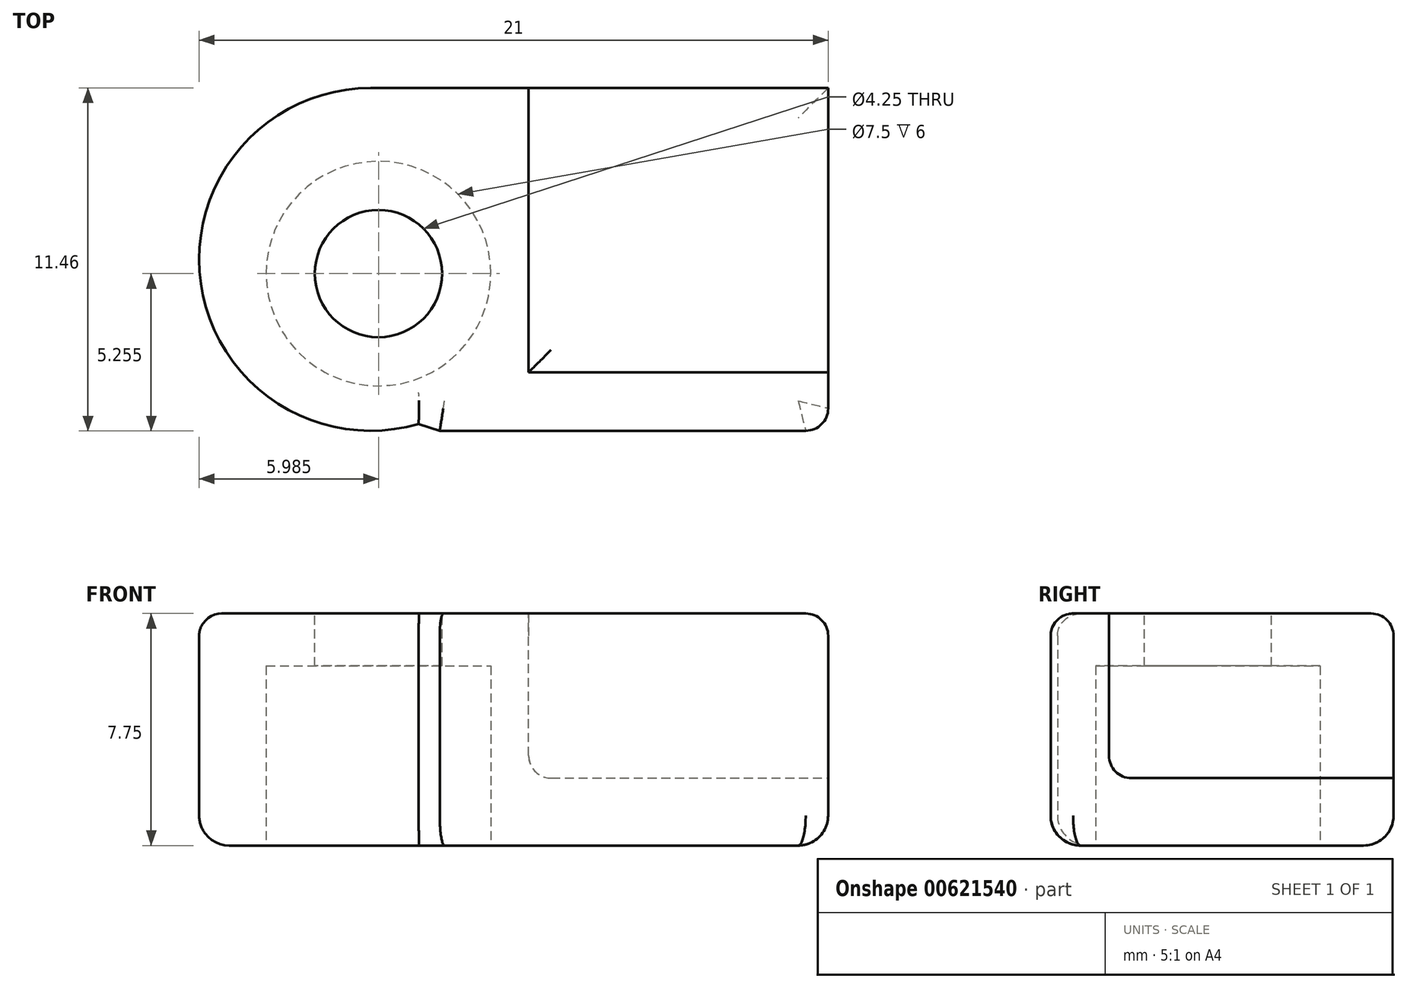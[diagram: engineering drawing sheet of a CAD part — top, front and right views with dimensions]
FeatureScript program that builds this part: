
annotation { "Feature Type Name" : "Feature", "Feature Type Description" : "" }
export const myFeature = defineFeature(function(context is Context, id is Id, definition is map)
    precondition{}
    {
        {
            var Q0;
            Q0=qCreatedBy(makeId("Top.planeOp"),FACE);
            var sketch = newSketch(context, id + "F0", { "sketchPlane" : qUnion([Q0])});
            skLineSegment(sketch, "E0.bottom", {"start": v(-6.14, -5.73) * mm, "end": v(6.83, -5.73) * mm});
            skLineSegment(sketch, "E0.top", {"start": v(-8.45, 5.73) * mm, "end": v(6.83, 5.73) * mm});
            skLineSegment(sketch, "E0.right", {"start": v(6.83, -5.73) * mm, "end": v(6.83, 5.73) * mm});
            skLineSegment(sketch, "E1", {"start": v(0, 23.22) * mm, "end": v(0, -32.08) * mm, "construction": true});
            skLineSegment(sketch, "E2", {"start": v(-40.7, 0) * mm, "end": v(47.24, 0) * mm, "construction": true});
            skArc(sketch, "E3", {"start": v(-8.45, 5.72) * mm, "mid": v(-14.11, -0.81) * mm, "end": v(-6.84, -5.5) * mm});
            skLineSegment(sketch, "E4", {"start": v(-6.84, -5.5) * mm, "end": v(-6.14, -5.73) * mm});
            skSolve(sketch);
        }
        {
            var Q0;
            Q0=makeQuery(id+"F0.imprint","IMPRINT",FACE,{"disambiguationData":[TD([[makeQuery(id+"F0.imprint","IMPRINT",EDGE,{"derivedFrom":sQuery(id+"F0.wireOp",EDGE,"E0.bottom")}),1.0]])]});
            extrude(context, id + "F1", {"entities" : qUnion([Q0]), "depth" : 7.75 * mm, "offsetDistance" : 25 * mm});
        }
        {
            var Q0;
            Q0=makeQuery(id+"F1.opExtrude","CAP_FACE",FACE,{"disambiguationData":[OSD([sQuery(id+"F0.wireOp",EDGE,"E0.bottom"),sQuery(id+"F0.wireOp",EDGE,"E0.top"),sQuery(id+"F0.wireOp",EDGE,"E0.right"),sQuery(id+"F0.wireOp",EDGE,"E3")])],"isStart":false});
            var sketch = newSketch(context, id + "F2", { "sketchPlane" : qUnion([Q0])});
            skCircle(sketch, "E5", {"center": v(-8.19, -0.48) * mm, "radius": 2.12 * mm});
            skSolve(sketch);
        }
        {
            var Q0;
            Q0=makeQuery(id+"F2.imprint","IMPRINT",FACE,{"disambiguationData":[TD([[makeQuery(id+"F2.imprint","IMPRINT",EDGE,{"derivedFrom":sQuery(id+"F2.wireOp",EDGE,"E5")}),1.0]])]});
            extrude(context, id + "F3", {"entities" : qUnion([Q0]), "operationType" : NewBodyOperationType.REMOVE, "endBound" : BoundingType.THROUGH_ALL, "oppositeDirection" : true, "depth" : 25 * mm, "offsetDistance" : 25 * mm});
        }
        {
            var Q0;
            Q0=makeQuery(id+"F1.opExtrude","CAP_FACE",FACE,{"disambiguationData":[OSD([sQuery(id+"F0.wireOp",EDGE,"E0.bottom"),sQuery(id+"F0.wireOp",EDGE,"E0.top"),sQuery(id+"F0.wireOp",EDGE,"E0.right"),sQuery(id+"F0.wireOp",EDGE,"E3")])],"isStart":false});
            var sketch = newSketch(context, id + "F4", { "sketchPlane" : qUnion([Q0])});
            skLineSegment(sketch, "E6.bottom", {"start": v(6.83, 5.73) * mm, "end": v(-3.17, 5.73) * mm});
            skLineSegment(sketch, "E6.top", {"start": v(6.83, -3.77) * mm, "end": v(-3.17, -3.77) * mm});
            skLineSegment(sketch, "E6.left", {"start": v(6.83, 5.73) * mm, "end": v(6.83, -3.77) * mm});
            skLineSegment(sketch, "E6.right", {"start": v(-3.17, 5.72) * mm, "end": v(-3.17, -3.77) * mm});
            skSolve(sketch);
        }
        {
            var Q0;
            Q0=makeQuery(id+"F4.imprint","IMPRINT",FACE,{"disambiguationData":[TD([[makeQuery(id+"F4.imprint","IMPRINT",EDGE,{"derivedFrom":sQuery(id+"F4.wireOp",EDGE,"E6.bottom")}),-1.0]])]});
            extrude(context, id + "F5", {"entities" : qUnion([Q0]), "operationType" : NewBodyOperationType.REMOVE, "oppositeDirection" : true, "depth" : 5.5 * mm, "offsetDistance" : 25 * mm});
        }
        {
            var Q0;
            Q0=makeQuery(id+"F1.opExtrude","CAP_FACE",FACE,{"disambiguationData":[OSD([sQuery(id+"F0.wireOp",EDGE,"E0.bottom"),sQuery(id+"F0.wireOp",EDGE,"E0.top"),sQuery(id+"F0.wireOp",EDGE,"E0.right"),sQuery(id+"F0.wireOp",EDGE,"E3")])],"isStart":true});
            var sketch = newSketch(context, id + "F6", { "sketchPlane" : qUnion([Q0])});
            skCircle(sketch, "E7", {"center": v(-8.19, 0.48) * mm, "radius": 3.75 * mm});
            skSolve(sketch);
        }
        {
            var Q0;
            Q0=makeQuery(id+"F6.imprint","IMPRINT",FACE,{"disambiguationData":[TD([[makeQuery(id+"F6.imprint","IMPRINT",EDGE,{"derivedFrom":sQuery(id+"F6.wireOp",EDGE,"E7")}),1.0]])]});
            extrude(context, id + "F7", {"entities" : qUnion([Q0]), "operationType" : NewBodyOperationType.REMOVE, "oppositeDirection" : true, "depth" : 6 * mm, "offsetDistance" : 25 * mm});
        }
        {
            var Q0;
            Q0=makeQuery(id+"F1.opExtrude","CAP_EDGE",EDGE,{"disambiguationData":[OSD([sQuery(id+"F0.wireOp",EDGE,"E0.top")])],"isStart":true});
            var Q1;
            Q1=makeQuery(id+"F1.opExtrude","CAP_EDGE",EDGE,{"disambiguationData":[OSD([sQuery(id+"F0.wireOp",EDGE,"E3")])],"isStart":true});
            var Q2;
            Q2=makeQuery(id+"F1.opExtrude","CAP_EDGE",EDGE,{"disambiguationData":[OSD([sQuery(id+"F0.wireOp",EDGE,"E4")])],"isStart":true});
            var Q3;
            Q3=makeQuery(id+"F1.opExtrude","CAP_EDGE",EDGE,{"disambiguationData":[OSD([sQuery(id+"F0.wireOp",EDGE,"E0.bottom")])],"isStart":true});
            var Q4;
            Q4=makeQuery(id+"F1.opExtrude","CAP_EDGE",EDGE,{"disambiguationData":[OSD([sQuery(id+"F0.wireOp",EDGE,"E0.right")])],"isStart":true});
            var Q5;
            Q5=makeQuery(id+"F7.boolean.opBoolean","COPY",EDGE,{"derivedFrom":makeQuery(id+"F7.opExtrude","CAP_EDGE",EDGE,{"disambiguationData":[OSD([sQuery(id+"F6.wireOp",EDGE,"E7")])],"isStart":true})});
            fillet(context, id + "F8", {"entities" : qUnion([Q0, Q1, Q2, Q3, Q4, Q5]), "radius" : 1 * mm, "allowEdgeOverflow" : false});
        }
        {
            var Q0;
            Q0=makeQuery(id+"F1.opExtrude","CAP_EDGE",EDGE,{"disambiguationData":[OSD([sQuery(id+"F0.wireOp",EDGE,"E3")])],"isStart":false});
            var Q1;
            Q1=makeQuery(id+"F1.opExtrude","CAP_EDGE",EDGE,{"disambiguationData":[OSD([sQuery(id+"F0.wireOp",EDGE,"E0.bottom")])],"isStart":false});
            var Q2;
            Q2=makeQuery(id+"F1.opExtrude","CAP_EDGE",EDGE,{"disambiguationData":[OSD([sQuery(id+"F0.wireOp",EDGE,"E4")])],"isStart":false});
            var Q3;
            Q3=makeQuery(id+"F1.opExtrude","CAP_EDGE",EDGE,{"disambiguationData":[OSD([sQuery(id+"F0.wireOp",EDGE,"E0.top")])],"isStart":false});
            var Q4;
            Q4=makeQuery(id+"F5.boolean.opBoolean","COPY",EDGE,{"derivedFrom":makeQuery(id+"F5.opExtrude","CAP_EDGE",EDGE,{"disambiguationData":[OSD([sQuery(id+"F4.wireOp",EDGE,"E6.right")])],"isStart":true})});
            var Q5;
            Q5=makeQuery(id+"F5.boolean.opBoolean","COPY",EDGE,{"derivedFrom":makeQuery(id+"F5.opExtrude","CAP_EDGE",EDGE,{"disambiguationData":[OSD([sQuery(id+"F4.wireOp",EDGE,"E6.top")])],"isStart":true})});
            var Q6;
            Q6=makeQuery(id+"F1.opExtrude","CAP_EDGE",EDGE,{"disambiguationData":[OSD([sQuery(id+"F0.wireOp",EDGE,"E0.right")])],"isStart":false});
            var Q7;
            Q7=makeQuery(id+"F5.boolean.opBoolean","COPY",EDGE,{"derivedFrom":makeQuery(id+"F5.opExtrude","CAP_EDGE",EDGE,{"disambiguationData":[OSD([sQuery(id+"F4.wireOp",EDGE,"E6.top")])],"isStart":false})});
            var Q8;
            Q8=makeQuery(id+"F5.boolean.opBoolean","COPY",EDGE,{"derivedFrom":makeQuery(id+"F5.opExtrude","CAP_EDGE",EDGE,{"disambiguationData":[OSD([sQuery(id+"F4.wireOp",EDGE,"E6.right")])],"isStart":false})});
            var Q9;
            Q9=makeQuery(id+"F5.boolean.opBoolean","COPY",EDGE,{"derivedFrom":makeQuery(id+"F5.opExtrude","CAP_EDGE",EDGE,{"disambiguationData":[OSD([sQuery(id+"F4.wireOp",EDGE,"E6.left")])],"isStart":false})});
            var Q10;
            Q10=makeQuery(id+"F5.boolean.opBoolean","COPY",EDGE,{"derivedFrom":makeQuery(id+"F5.opExtrude","CAP_EDGE",EDGE,{"disambiguationData":[OSD([sQuery(id+"F4.wireOp",EDGE,"E6.bottom")])],"isStart":false})});
            var Q11;
            Q11=makeQuery(id+"F1.opExtrude","SWEPT_EDGE",EDGE,{"disambiguationData":[OSD([sQuery(id+"F0.wireOp",EDGE,"E0.bottom"),sQuery(id+"F0.wireOp",EDGE,"E0.right")])]});
            fillet(context, id + "F9", {"entities" : qUnion([Q0, Q1, Q2, Q3, Q4, Q5, Q6, Q7, Q8, Q9, Q10, Q11]), "radius" : 0.75 * mm, "tangentPropagation" : true, "allowEdgeOverflow" : false});
        }
    });
